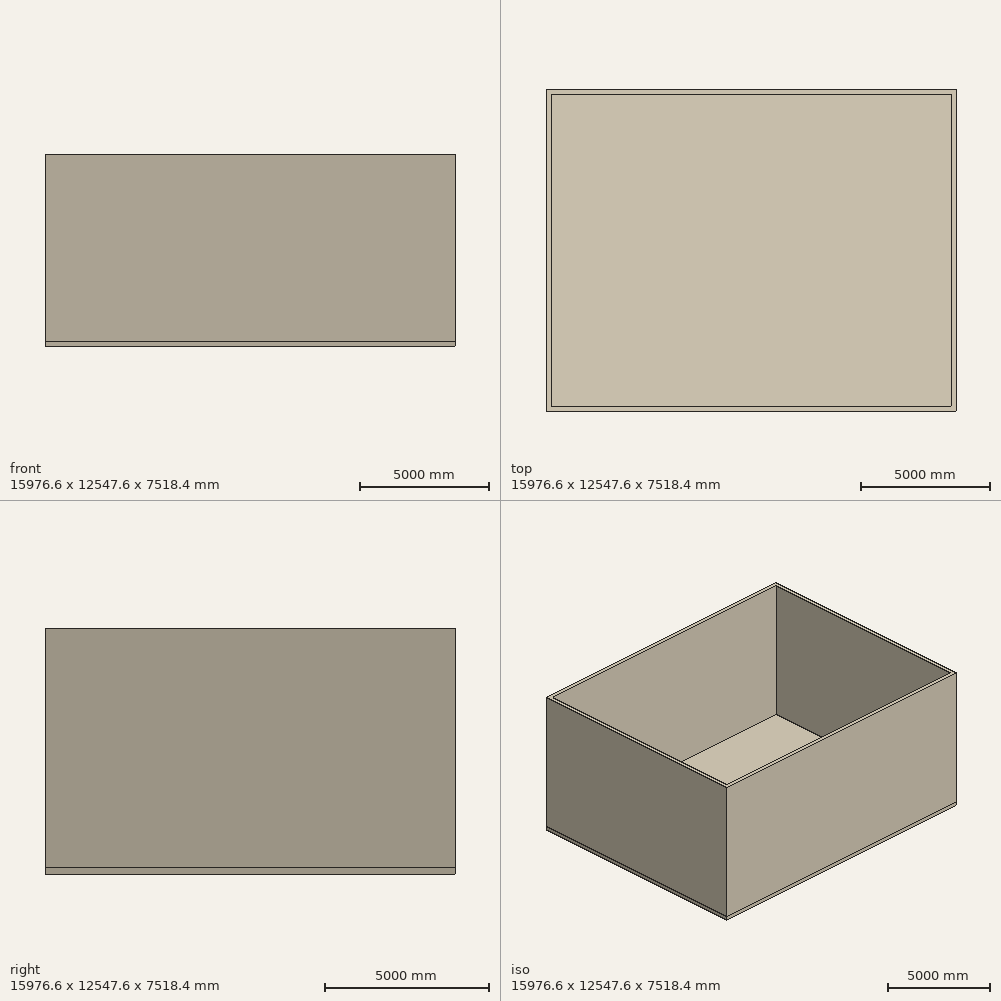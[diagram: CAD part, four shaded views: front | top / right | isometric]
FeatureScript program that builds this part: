
annotation { "Feature Type Name" : "Feature", "Feature Type Description" : "" }
export const myFeature = defineFeature(function(context is Context, id is Id, definition is map)
    precondition{}
    {
        {
            var Q0;
            Q0=qCreatedBy(makeId("Top.planeOp"),FACE);
            var sketch = newSketch(context, id + "F0", { "sketchPlane" : qUnion([Q0])});
            skLineSegment(sketch, "E0.bottom", {"start": v(-7589.92, 5794.46) * mm, "end": v(7980.28, 5794.46) * mm});
            skLineSegment(sketch, "E0.top", {"start": v(-7589.92, -6346.74) * mm, "end": v(7980.28, -6346.74) * mm});
            skLineSegment(sketch, "E0.left", {"start": v(-7589.92, 5794.46) * mm, "end": v(-7589.92, -6346.74) * mm});
            skLineSegment(sketch, "E0.right", {"start": v(7980.28, 5794.46) * mm, "end": v(7980.28, -6346.74) * mm});
            skLineSegment(sketch, "E1.0", {"start": v(-7793.12, 5997.66) * mm, "end": v(8183.48, 5997.66) * mm});
            skLineSegment(sketch, "E1.1", {"start": v(-7793.12, 5997.66) * mm, "end": v(-7793.12, -6549.94) * mm});
            skLineSegment(sketch, "E1.2", {"start": v(-7793.12, -6549.94) * mm, "end": v(8183.48, -6549.94) * mm});
            skLineSegment(sketch, "E1.3", {"start": v(8183.48, 5997.66) * mm, "end": v(8183.48, -6549.94) * mm});
            skCircle(sketch, "E2", {"center": v(6405.48, 3762.46) * mm, "radius": 1143 * mm});
            skLineSegment(sketch, "E3", {"start": v(-9206.83, 3762.46) * mm, "end": v(10238.57, 3762.46) * mm, "construction": true});
            skCircle(sketch, "E4", {"center": v(2112.88, 3762.46) * mm, "radius": 1143 * mm});
            skCircle(sketch, "E5", {"center": v(-3779.92, 3762.46) * mm, "radius": 1143 * mm});
            skPoint(sketch, "E6", {"position": v(-1316.12, 3762.46) * mm});
            skPoint(sketch, "E7", {"position": v(-2636.92, 3762.46) * mm});
            skPoint(sketch, "E8", {"position": v(-655.72, 3762.46) * mm});
            skLineSegment(sketch, "E9", {"start": v(5262.48, 8977.4) * mm, "end": v(5262.48, 1272.2) * mm, "construction": true});
            skLineSegment(sketch, "E10", {"start": v(-4922.92, 9010.2) * mm, "end": v(-4922.92, 1364.1) * mm, "construction": true});
            skSolve(sketch);
        }
        {
            var Q0;
            Q0=makeQuery(id+"F0.imprint","IMPRINT",FACE,{"disambiguationData":[TD([[makeQuery(id+"F0.imprint","IMPRINT",EDGE,{"derivedFrom":sQuery(id+"F0.wireOp",EDGE,"E0.bottom")}),1.0]])]});
            extrude(context, id + "F1", {"entities" : qUnion([Q0]), "depth" : 7315.2 * mm});
        }
        {
            var Q0;
            Q0=makeQuery(id+"F0.imprint","IMPRINT",FACE,{"disambiguationData":[TD([[makeQuery(id+"F0.imprint","IMPRINT",EDGE,{"derivedFrom":sQuery(id+"F0.wireOp",EDGE,"E0.bottom")}),1.0]])]});
            extrude(context, id + "F2", {"entities" : qUnion([Q0]), "oppositeDirection" : true, "depth" : 203.2 * mm});
        }
        {
            var Q0;
            Q0=makeQuery(id+"F0.imprint","IMPRINT",FACE,{"disambiguationData":[TD([[makeQuery(id+"F0.imprint","IMPRINT",EDGE,{"derivedFrom":sQuery(id+"F0.wireOp",EDGE,"E0.bottom")}),-1.0]])]});
            var Q1;
            Q1=makeQuery(id+"F0.imprint","IMPRINT",FACE,{"disambiguationData":[TD([[makeQuery(id+"F0.imprint","IMPRINT",EDGE,{"derivedFrom":sQuery(id+"F0.wireOp",EDGE,"E5")}),1.0]])]});
            var Q2;
            Q2=makeQuery(id+"F0.imprint","IMPRINT",FACE,{"disambiguationData":[TD([[makeQuery(id+"F0.imprint","IMPRINT",EDGE,{"derivedFrom":sQuery(id+"F0.wireOp",EDGE,"E4")}),1.0]])]});
            var Q3;
            Q3=makeQuery(id+"F0.imprint","IMPRINT",FACE,{"disambiguationData":[TD([[makeQuery(id+"F0.imprint","IMPRINT",EDGE,{"derivedFrom":sQuery(id+"F0.wireOp",EDGE,"E2")}),1.0]])]});
            extrude(context, id + "F3", {"entities" : qUnion([Q0, Q1, Q2, Q3]), "oppositeDirection" : true, "depth" : 127 * mm});
        }
        {
            var Q0;
            Q0=sQuery(id+"F0.wireOp",EDGE,"E10");
            var Q1;
            Q1=sQuery(id+"F0.wireOp",EDGE,"E1.0");
            cPlane(context, id + "F4", {"entities" : qUnion([Q0, Q1]), "cplaneType" : CPlaneType.LINE_ANGLE, "offset" : 25.4 * mm, "angle" : 90 * degree, "width" : 152.4 * mm, "height" : 152.4 * mm});
        }
        {
            var Q0;
            Q0=qCreatedBy(id+"F4.planeOp",FACE);
            var sketch = newSketch(context, id + "F5", { "sketchPlane" : qUnion([Q0])});
            skPoint(sketch, "E11.0", {"position": v(-5794.46, 0) * mm});
            skLineSegment(sketch, "E12", {"start": v(-5794.46, 0) * mm, "end": v(-5794.46, 1219.2) * mm, "construction": true});
            skSolve(sketch);
        }
        {
            var Q0;
            Q0=makeQuery(id+"F1.opExtrude","SWEPT_FACE",FACE,{"disambiguationData":[OSD([sQuery(id+"F0.wireOp",EDGE,"E0.bottom")])]});
            var sketch = newSketch(context, id + "F6", { "sketchPlane" : qUnion([Q0])});
            skLineSegment(sketch, "E13.0", {"start": v(-4922.92, 0) * mm, "end": v(-4922.92, 1219.2) * mm});
            skSolve(sketch);
        }
    });
